# Revit family: Haworth_Masters_Wardrobe_OpenCabinet
name_source: partatom
category: Furniture Systems
revit_build: Autodesk Revit 2018 (Build: 20170223_1515(x64)
units: mm (PartAtom-declared; Revit-internal decimal feet)

## family parameters
Always vertical = Yes
Cut with Voids When Loaded = No
OmniClass Number = 23.40.70.14.64.21
OmniClass Title = Systems Furniture
Part Type = Normal
Room Calculation Point = No
Round Connector Dimension = Use Diameter
Shared = No
Work Plane-Based = No

## types (7) — shared parameters
Assembly Code = E2020200
Bar Pull = No
Bar Pull Length = 30"
Base Height = 3"
Classic Pull = Yes
Description = Haworth - Masters - Wardrobe - Open Cabinet
Door Finish = Haworth _ Wood _ White Oak
Door Pull Offset = 1 1/2"
Finger Pull = No
Fixed Shelf Height = 24 5/8"
Linear Pull = No
Lock Offset Centerline = 3"
Manufacturer = Haworth
Max. Height = 81 5/8"
Max. Width = 36"
Min. Height = 69"
Min. Width = 30"
Model = Haworth - Masters - Wardrobe - Open Cabinet
Panel Finish = Haworth _ Wood _ White Oak
Panel Thickness = 3/4"
Pull Finish = Haworth _ Metal _ Brushed Aluminum
Pull Height Centerline = 35"
Pull Offset Centerline = 3"
Revision Number = 5
Size = Verify Final Dim. w/ Haworth
Sustainability Info = http://www.haworth.com
URL = www.haworth.com
URL - Product = http://www.haworth.com
Warranty = http://www.haworth.com

## per-type parameters (varying)
| type | # of Shelves | 19in. Depth | 24in. Depth | 30in. Width | 36in. Width | 69in. Height | 82in. Height | Actual Depth | Actual Height | Actual Width | Door Height | Door Width | Shelf Depth | Shelf Spacing | Shelf Width |
| 36w 19d 82h | 4 | Yes | No | No | Yes | No | Yes | 19" | 81 5/8" | 36" | 78 5/8" | 18 3/8" | 17 1/2" | 11 45/256" | 16 7/8" |
| 30w 19d 69h | 3 | Yes | No | Yes | No | Yes | No | 19" | 69" | 30" | 66" | 15 3/8" | 17 1/2" | 10 13/16" | 13 7/8" |
| 30w 24d 69h | 3 | No | Yes | Yes | No | Yes | No | 24" | 69" | 30" | 66" | 15 3/8" | 22 1/2" | 10 13/16" | 13 7/8" |
| 30w 24d 82h | 4 | No | Yes | Yes | No | No | Yes | 24" | 81 5/8" | 30" | 78 5/8" | 15 3/8" | 22 1/2" | 11 45/256" | 13 7/8" |
| 30w 19d 82h | 4 | Yes | No | Yes | No | No | Yes | 19" | 81 5/8" | 30" | 78 5/8" | 15 3/8" | 17 1/2" | 11 45/256" | 13 7/8" |
| 36w 24d 69h | 3 | No | Yes | No | Yes | Yes | No | 24" | 69" | 36" | 66" | 18 3/8" | 22 1/2" | 10 13/16" | 16 7/8" |
| 36w 19d 69h | 3 | Yes | No | No | Yes | Yes | No | 19" | 69" | 36" | 66" | 18 3/8" | 17 1/2" | 10 13/16" | 16 7/8" |

## geometry (parser evidence)
native form markers: Sweep x10
no freeform markers — native parametric forms only
